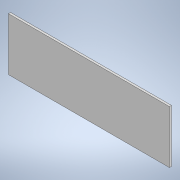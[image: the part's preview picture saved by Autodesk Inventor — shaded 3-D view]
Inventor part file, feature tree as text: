
AUTODESK INVENTOR PART (.ipt)
format: ipt  version: 2021 (Build 250183000, 183)  size: 96,256 bytes
history: native  units: in
note: dims shown in document units (in); Inventor stores cm internally (conversion verified against a paired STEP export)
features: extrude x1, sketch x1
ambient origin geometry x8: Origin, YZ Plane, XZ Plane, XY Plane, X Axis, Y Axis, Z Axis, Center Point
bodies: Solid1 (feature_tree)
feature tree (2):
  extrude  "Extrusion1"  Depth=0.9843in
  sketch  "Sketch1"  dims[d0=3.0in d1=0.9843in d2=0.0394in d3=0.0in]
